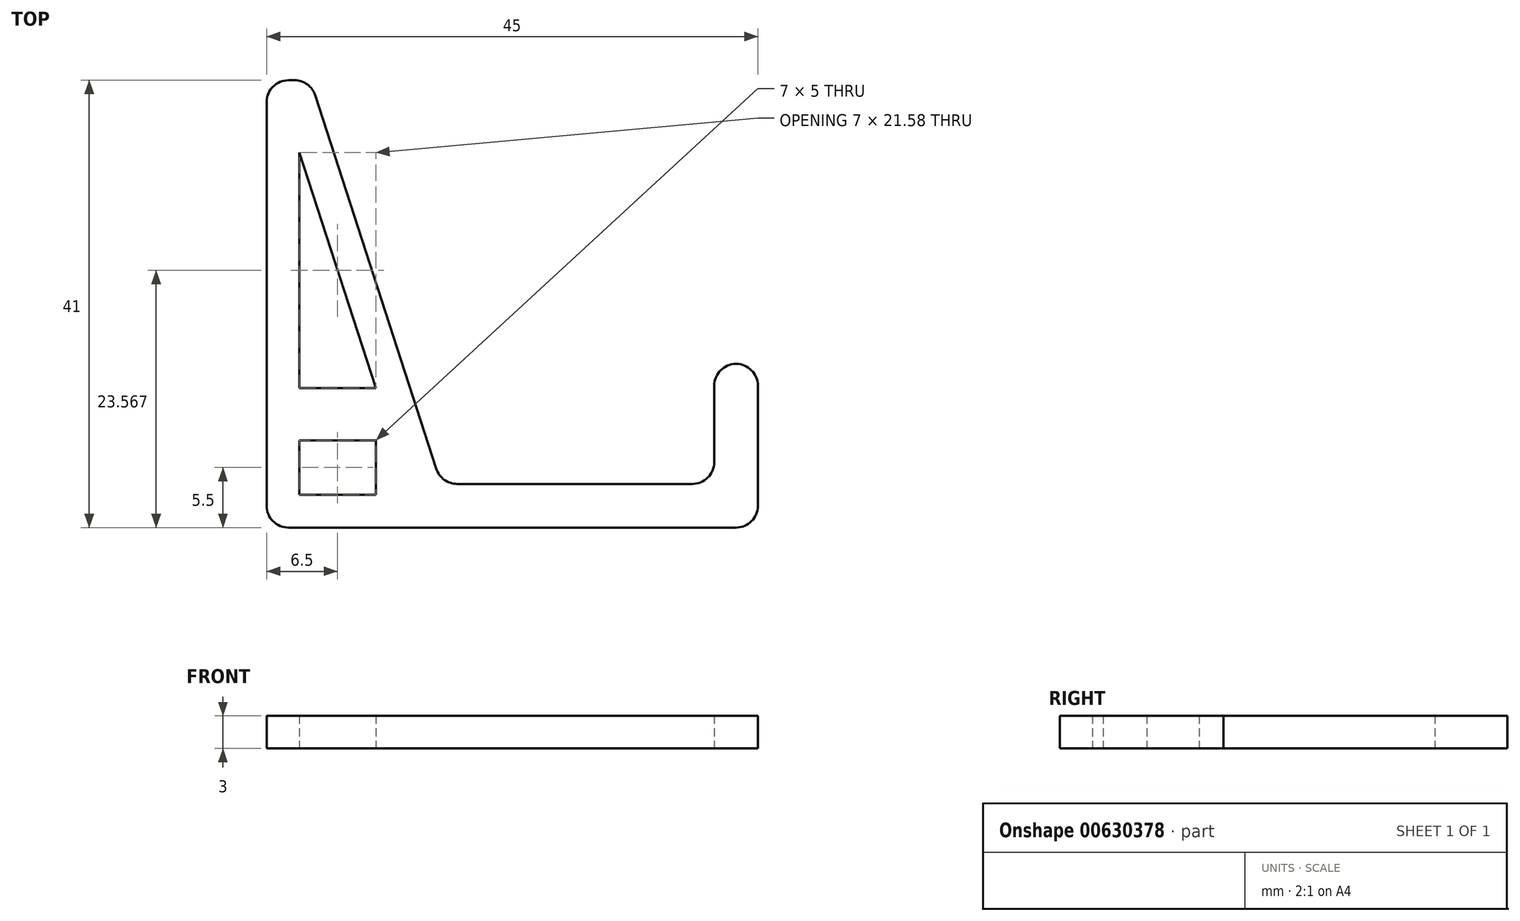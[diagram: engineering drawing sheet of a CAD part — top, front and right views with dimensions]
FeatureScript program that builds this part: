
annotation { "Feature Type Name" : "Feature", "Feature Type Description" : "" }
export const myFeature = defineFeature(function(context is Context, id is Id, definition is map)
    precondition{}
    {
        {
            var Q0;
            Q0=qCreatedBy(makeId("Top.planeOp"),FACE);
            var sketch = newSketch(context, id + "F0", { "sketchPlane" : qUnion([Q0])});
            skLineSegment(sketch, "E0", {"start": v(0, 0) * mm, "end": v(25, 0) * mm});
            skLineSegment(sketch, "E1", {"start": v(25, 0) * mm, "end": v(25, 11) * mm});
            skLineSegment(sketch, "E2", {"start": v(29, -4) * mm, "end": v(-16, -4) * mm});
            skLineSegment(sketch, "E3", {"start": v(-16, -4) * mm, "end": v(-16, 37) * mm});
            skLineSegment(sketch, "E4.bottom", {"start": v(-13, 4) * mm, "end": v(-6, 4) * mm});
            skLineSegment(sketch, "E4.top", {"start": v(-13, -1) * mm, "end": v(-6, -1) * mm});
            skLineSegment(sketch, "E4.left", {"start": v(-13, 4) * mm, "end": v(-13, -1) * mm});
            skLineSegment(sketch, "E4.right", {"start": v(-6, 4) * mm, "end": v(-6, -1) * mm});
            skLineSegment(sketch, "E5", {"start": v(-16, 37) * mm, "end": v(-12, 37) * mm});
            skLineSegment(sketch, "E6", {"start": v(-12, 37) * mm, "end": v(0, 0) * mm});
            skLineSegment(sketch, "E7", {"start": v(-13, 30.36) * mm, "end": v(-6, 8.78) * mm});
            skLineSegment(sketch, "E8", {"start": v(-6, 8.78) * mm, "end": v(-13, 8.78) * mm});
            skLineSegment(sketch, "E9", {"start": v(-13, 8.78) * mm, "end": v(-13, 30.36) * mm});
            skLineSegment(sketch, "E10", {"start": v(25, 11) * mm, "end": v(29, 11) * mm});
            skLineSegment(sketch, "E11", {"start": v(29, 11) * mm, "end": v(29, -4) * mm});
            skSolve(sketch);
        }
        {
            var Q0;
            Q0 = qSketchRegion(id + "F0", true);
            extrude(context, id + "F1", {"entities" : qUnion([Q0]), "depth" : 3 * mm, "offsetDistance" : 25 * mm});
        }
        {
            var Q0;
            Q0=makeQuery(id+"F1.opExtrude","SWEPT_EDGE",EDGE,{"disambiguationData":[OSD([sQuery(id+"F0.wireOp",EDGE,"E3"),sQuery(id+"F0.wireOp",EDGE,"VJwZyPKZ-cRsQ-hwfR-Dsfz-vjPZ57zVgOYD")])]});
            var Q1;
            Q1=makeQuery(id+"F1.opExtrude","SWEPT_EDGE",EDGE,{"disambiguationData":[OSD([sQuery(id+"F0.wireOp",EDGE,"E2"),sQuery(id+"F0.wireOp",EDGE,"E3")])]});
            var Q2;
            Q2=makeQuery(id+"F1.opExtrude","SWEPT_EDGE",EDGE,{"disambiguationData":[OSD([sQuery(id+"F0.wireOp",EDGE,"E0"),sQuery(id+"F0.wireOp",EDGE,"KLTCBtqQ-Dt2S-ciAo-lRLo-qQiTnvAzSNqK")])]});
            var Q3;
            Q3=makeQuery(id+"F1.opExtrude","SWEPT_EDGE",EDGE,{"disambiguationData":[OSD([sQuery(id+"F0.wireOp",EDGE,"E1"),sQuery(id+"F0.wireOp",EDGE,"ISqY7byC-DNOo-f94A-jyvQ-YiXSVBw7dL1w")])]});
            var Q4;
            Q4=makeQuery(id+"F1.opExtrude","SWEPT_EDGE",EDGE,{"disambiguationData":[OSD([sQuery(id+"F0.wireOp",EDGE,"KLTCBtqQ-Dt2S-ciAo-lRLo-qQiTnvAzSNqK"),sQuery(id+"F0.wireOp",EDGE,"VJwZyPKZ-cRsQ-hwfR-Dsfz-vjPZ57zVgOYD")])]});
            var Q5;
            Q5=makeQuery(id+"F1.opExtrude","SWEPT_EDGE",EDGE,{"disambiguationData":[OSD([sQuery(id+"F0.wireOp",EDGE,"E0"),sQuery(id+"F0.wireOp",EDGE,"E1")])]});
            var Q6;
            Q6=makeQuery(id+"F1.opExtrude","SWEPT_EDGE",EDGE,{"disambiguationData":[OSD([sQuery(id+"F0.wireOp",EDGE,"j3oL4dly-Z7X1-UHMZ-EDmt-8N80seh04TxN"),sQuery(id+"F0.wireOp",EDGE,"E2")])]});
            var Q7;
            Q7=makeQuery(id+"F1.opExtrude","SWEPT_EDGE",EDGE,{"disambiguationData":[OSD([sQuery(id+"F0.wireOp",EDGE,"E5"),sQuery(id+"F0.wireOp",EDGE,"E6")])]});
            var Q8;
            Q8=makeQuery(id+"F1.opExtrude","SWEPT_EDGE",EDGE,{"disambiguationData":[OSD([sQuery(id+"F0.wireOp",EDGE,"E10"),sQuery(id+"F0.wireOp",EDGE,"E11")])]});
            fillet(context, id + "F2", {"entities" : qUnion([Q0, Q1, Q2, Q3, Q4, Q5, Q6, Q7, Q8]), "radius" : 2 * mm, "tangentPropagation" : true, "allowEdgeOverflow" : false});
        }
    });
